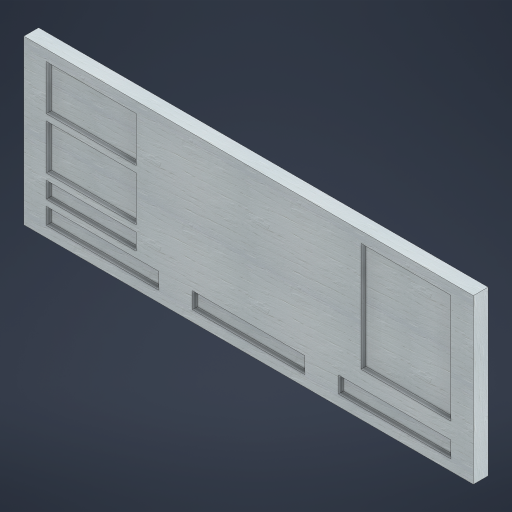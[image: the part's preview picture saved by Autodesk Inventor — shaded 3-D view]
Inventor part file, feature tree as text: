
AUTODESK INVENTOR PART (.ipt)
format: ipt  version: 2024 (Build 280153000, 153)  size: 421,376 bytes
history: native  units: mm
features: extrude x3, other x1, sketch x1
ambient origin geometry x8: Origin, YZ Plane, XZ Plane, XY Plane, X Axis, Y Axis, Z Axis, Center Point
bodies: Body1 (feature_tree)
feature tree (5):
  other  "Sólido1"
  extrude  "Extrusión1"  Depth=137.5mm
  extrude  "Extrusión2"  Depth=20.0mm
  extrude  "Extrusión3"  Depth=27.5mm
  sketch  "Boceto2"  dims[d3=0.0mm d4=137.5mm d5=20.0mm d6=27.5mm d7=137.5mm d8=20.0mm d9=27.5mm d10=13.333333mm d11=13.333333mm d12=137.5mm d13=41.25mm d14=41.25mm d15=20.0mm d17=110.0mm d18=133.333333mm d19=27.5mm d20=13.333333mm d21=110.0mm d22=55.0mm d23=27.5mm d24=13.333333mm d25=110.0mm d26=55.0mm d27=27.5mm d28=7.843137mm d29=110.0mm d30=20.0mm d31=7.843137mm d32=7.647059mm d33=6.0mm d34=0.0mm d35=9.0mm d36=9.0mm d37=9.0mm d38=9.0mm d39=9.0mm d40=66.666667mm d41=9.0mm d42=66.666667mm d43=9.0mm d44=66.666667mm d45=9.0mm d46=66.666667mm d47=6.0mm d48=0.0mm]
